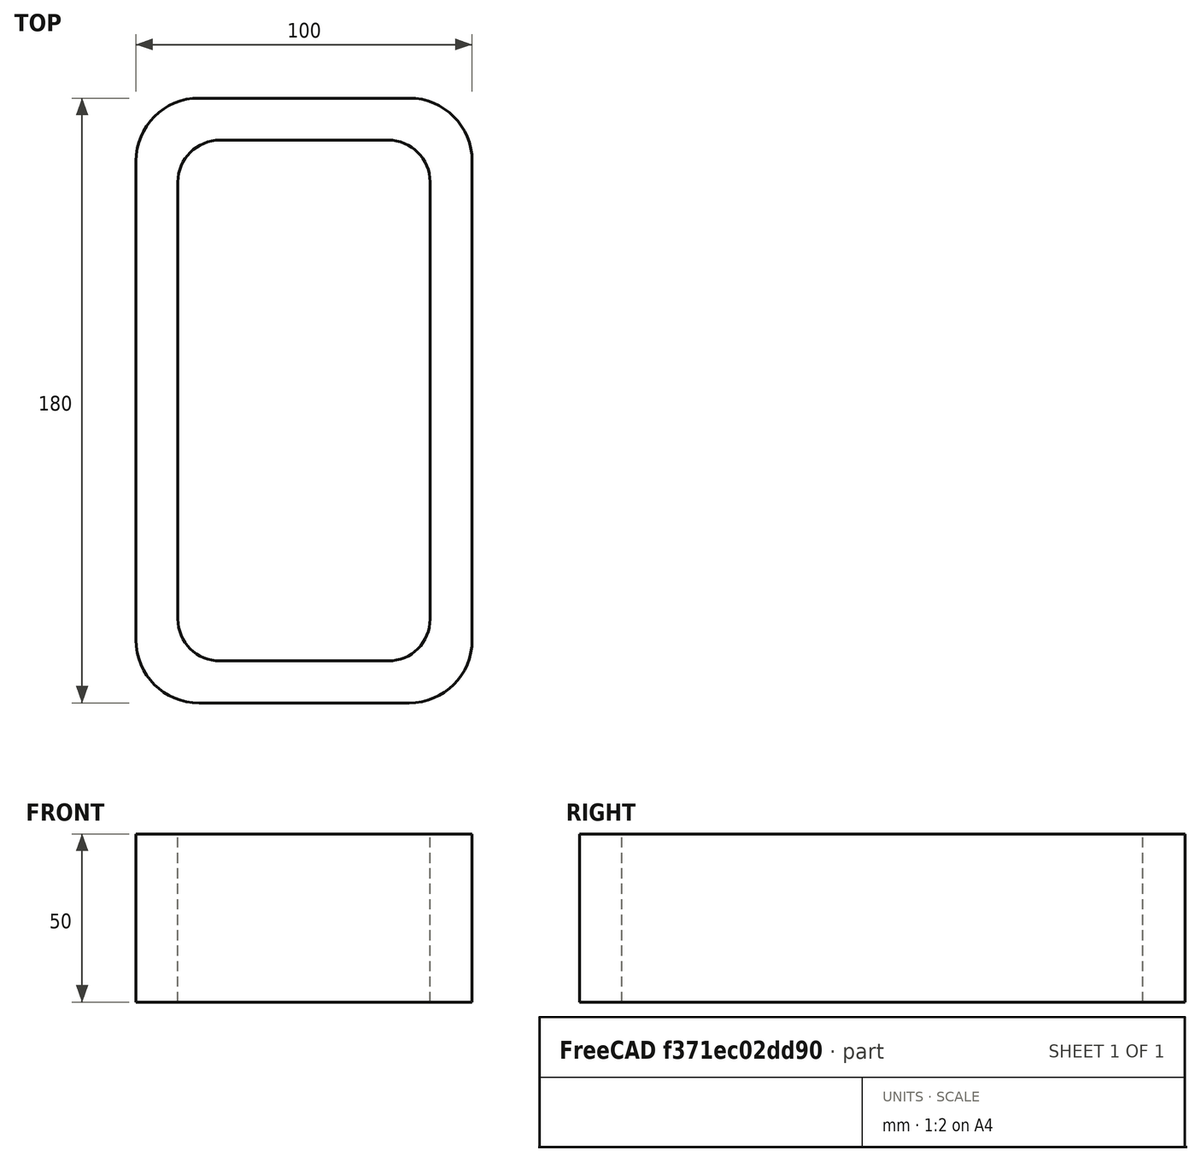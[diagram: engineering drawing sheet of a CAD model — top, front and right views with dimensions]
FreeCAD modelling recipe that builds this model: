
FCSTD DOCUMENT  (FreeCAD 0.15R4671 (Git))
Label: Rectangular hollow section 180x100x12.5 EN10219 S235JRH
License: All rights reserved
LicenseURL: http://en.wikipedia.org/wiki/All_rights_reserved
objects: Sketcher::SketchObject×1, Part::Extrusion×1
note: 2 computed .brp shape members not serialized (recipe doc carries the construction recipe); baked Part::Feature solids carry a one-line shape summary decoded from their .brp

FEATURE [Sketcher::SketchObject] Sketch
  sketch-geometry (16):
    g0: LineSegment StartX=-25 StartY=77.5 StartZ=0 EndX=25 EndY=77.5 EndZ=0
    g1: LineSegment StartX=37.5 StartY=65 StartZ=0 EndX=37.5 EndY=-65 EndZ=0
    g2: LineSegment StartX=25 StartY=-77.5 StartZ=0 EndX=-25 EndY=-77.5 EndZ=0
    g3: LineSegment StartX=-37.5 StartY=-65 StartZ=0 EndX=-37.5 EndY=65 EndZ=0
    g4: LineSegment StartX=-31.25 StartY=90 StartZ=0 EndX=31.25 EndY=90 EndZ=0
    g5: LineSegment StartX=50 StartY=71.25 StartZ=0 EndX=50 EndY=-71.25 EndZ=0
    g6: LineSegment StartX=31.25 StartY=-90 StartZ=0 EndX=-31.25 EndY=-90 EndZ=0
    g7: LineSegment StartX=-50 StartY=-71.25 StartZ=0 EndX=-50 EndY=71.25 EndZ=0
    g8: ArcOfCircle CenterX=-25 CenterY=65 CenterZ=0 NormalX=0 NormalY=0 NormalZ=1 Radius=12.5 StartAngle=1.5708 EndAngle=3.14159
    g9: ArcOfCircle CenterX=25 CenterY=65 CenterZ=0 NormalX=0 NormalY=0 NormalZ=1 Radius=12.5 StartAngle=0 EndAngle=1.5708
    g10: ArcOfCircle CenterX=25 CenterY=-65 CenterZ=0 NormalX=0 NormalY=0 NormalZ=1 Radius=12.5 StartAngle=4.71239 EndAngle=6.28319
    g11: ArcOfCircle CenterX=-25 CenterY=-65 CenterZ=0 NormalX=0 NormalY=0 NormalZ=1 Radius=12.5 StartAngle=3.14159 EndAngle=4.71239
    g12: ArcOfCircle CenterX=31.25 CenterY=71.25 CenterZ=0 NormalX=0 NormalY=0 NormalZ=1 Radius=18.75 StartAngle=0 EndAngle=1.5708
    g13: ArcOfCircle CenterX=31.25 CenterY=-71.25 CenterZ=0 NormalX=0 NormalY=0 NormalZ=1 Radius=18.75 StartAngle=4.71239 EndAngle=6.28319
    g14: ArcOfCircle CenterX=-31.25 CenterY=-71.25 CenterZ=0 NormalX=0 NormalY=0 NormalZ=1 Radius=18.75 StartAngle=3.14159 EndAngle=4.71239
    g15: ArcOfCircle CenterX=-31.25 CenterY=71.25 CenterZ=0 NormalX=0 NormalY=0 NormalZ=1 Radius=18.75 StartAngle=1.5708 EndAngle=3.14159
  constraints (36):
    c: Horizontal(g2)
    c: Vertical(g3)
    c: Horizontal(g6)
    c: Vertical(g7)
    c: Tangent(g3,g8) = 1.5708
    c: Tangent(g0,g8) = 1.5708
    c: Tangent(g0,g9) = 1.5708
    c: Tangent(g1,g9) = 1.5708
    c: Tangent(g1,g10) = 1.5708
    c: Tangent(g2,g10) = 1.5708
    c: Tangent(g2,g11) = 1.5708
    c: Tangent(g3,g11) = 1.5708
    c: Tangent(g4,g12) = 1.5708
    c: Tangent(g5,g12) = 1.5708
    c: Tangent(g5,g13) = 1.5708
    c: Tangent(g6,g13) = 1.5708
    c: Tangent(g6,g14) = 1.5708
    c: Tangent(g7,g14) = 1.5708
    c: Tangent(g7,g15) = 1.5708
    c: Tangent(g4,g15) = 1.5708
    c: Equal(g9,g8)
    c: Equal(g9,g11)
    c: Equal(g9,g10)
    c: Equal(g12,g15)
    c: Equal(g12,g14)
    c: Equal(g12,g13)
    c: Symmetric(g4,g6,g-1)
    c: Symmetric(g7,g5,g-2)
    c: DistanceY(g4,g6) = -180
    c: DistanceX(g7,g5) = 100
    c: Symmetric(g3,g1,g-2)
    c: Symmetric(g0,g2,g-1)
    c: DistanceY(g0,g4) = 12.5
    c: DistanceX(g5,g1) = -12.5
    c: Radius(g9) = 12.5
    c: Radius(g12) = 18.75
FEATURE [Part::Extrusion] Extrude  label="Rectangular hollow section 180x100x12.5 EN10219 S235JRH"
  Base = -> Sketch
  Dir = (0,0,50)
  Solid = true
